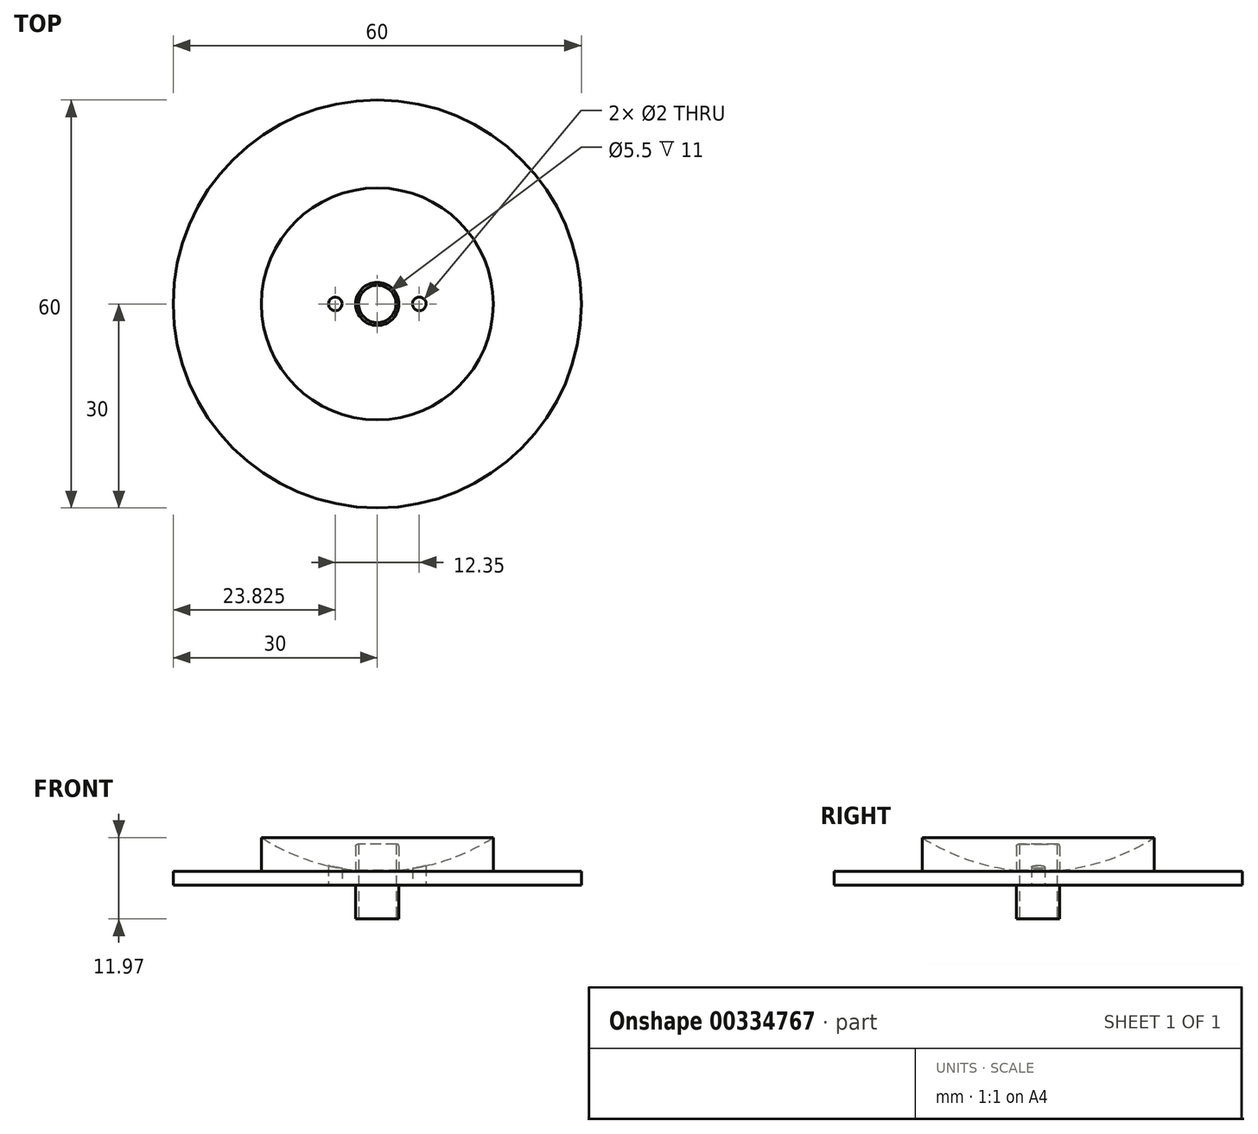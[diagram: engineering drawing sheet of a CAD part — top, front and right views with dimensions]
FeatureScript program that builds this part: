
annotation { "Feature Type Name" : "Feature", "Feature Type Description" : "" }
export const myFeature = defineFeature(function(context is Context, id is Id, definition is map)
    precondition{}
    {
        {
            var Q0;
            Q0=qCreatedBy(makeId("Front.planeOp"),FACE);
            var sketch = newSketch(context, id + "F0", { "sketchPlane" : qUnion([Q0])});
            skLineSegment(sketch, "E0.bottom", {"start": v(-30, 0) * mm, "end": v(30, 0) * mm});
            skLineSegment(sketch, "E0.top", {"start": v(-30, 2) * mm, "end": v(30, 2) * mm});
            skLineSegment(sketch, "E0.left", {"start": v(-30, 0) * mm, "end": v(-30, 2) * mm});
            skLineSegment(sketch, "E0.right", {"start": v(30, 0) * mm, "end": v(30, 2) * mm});
            skArc(sketch, "E1", {"start": v(-17.05, 6.97) * mm, "mid": v(0, 2) * mm, "end": v(17.05, 6.97) * mm});
            skLineSegment(sketch, "E2", {"start": v(-17.05, 6.97) * mm, "end": v(-17.05, 2) * mm});
            skLineSegment(sketch, "E3.MirrorCS", {"start": v(17.05, 6.97) * mm, "end": v(17.05, 2) * mm});
            skLineSegment(sketch, "E4", {"start": v(0, 65.5) * mm, "end": v(0, 0) * mm});
            skCircle(sketch, "E5", {"center": v(0, 33.75) * mm, "radius": 31.75 * mm});
            skSolve(sketch);
        }
        {
            var Q0;
            {var subQ0=sQuery(id+"F0.wireOp",EDGE,"E1");var subQ1=makeQuery(id+"F0.imprint","INTERSECT",VERTEX,{"derivedFrom":[subQ0,sQuery(id+"F0.wireOp",EDGE,"E3.MirrorCS")]});Q0=makeQuery(id+"F0.imprint","IMPRINT",FACE,{"disambiguationData":[TD([[makeQuery(id+"F0.imprint","IMPRINT",EDGE,{"disambiguationData":[TD([[subQ1,-1.0]])],"derivedFrom":subQ0}),1.0]])]});}
            var Q1;
            {var subQ0=sQuery(id+"F0.wireOp",EDGE,"E3.MirrorCS");Q1=makeQuery(id+"F0.imprint","IMPRINT",FACE,{"disambiguationData":[TD([[makeQuery(id+"F0.imprint","IMPRINT",EDGE,{"derivedFrom":subQ0}),-1.0]])]});}
            var Q2;
            {var subQ0=sQuery(id+"F0.wireOp",EDGE,"E0.right");Q2=makeQuery(id+"F0.imprint","IMPRINT",FACE,{"disambiguationData":[TD([[makeQuery(id+"F0.imprint","IMPRINT",EDGE,{"derivedFrom":subQ0}),1.0]])]});}
            var Q3;
            Q3=sQuery(id+"F0.wireOp",EDGE,"E4");
            revolve(context, id + "F1", {"entities" : qUnion([Q0, Q1, Q2]), "axis" : qUnion([Q3]), "revolveType" : RevolveType.FULL});
        }
        {
            var Q0;
            Q0=qCreatedBy(makeId("Top.planeOp"),FACE);
            var sketch = newSketch(context, id + "F2", { "sketchPlane" : qUnion([Q0])});
            skCircle(sketch, "E6", {"center": v(0, 0) * mm, "radius": 3.17 * mm});
            skCircle(sketch, "E7", {"center": v(0, 0) * mm, "radius": 2.75 * mm});
            skSolve(sketch);
        }
        {
            var Q0;
            Q0 = qSketchRegion(id + "F2", true);
            extrude(context, id + "F3", {"entities" : qUnion([Q0]), "operationType" : NewBodyOperationType.ADD, "depth" : 6 * mm, "hasSecondDirection" : true, "secondDirectionOppositeDirection" : true, "secondDirectionDepth" : 5 * mm});
        }
        {
            var Q0;
            Q0=makeQuery(id+"F3.opExtrude","CAP_EDGE",EDGE,{"disambiguationData":[OSD([sQuery(id+"F2.wireOp",EDGE,"E6")])],"isStart":false});
            fillet(context, id + "F4", {"entities" : qUnion([Q0]), "radius" : .3 * mm, "tangentPropagation" : true, "allowEdgeOverflow" : false});
        }
        {
            var Q0;
            Q0=makeQuery(id+"F3.boolean.opBoolean","SPLIT",FACE,{"disambiguationData":[TD([makeQuery(id+"F3.opExtrude","SWEPT_FACE",FACE,{"disambiguationData":[OSD([sQuery(id+"F2.wireOp",EDGE,"E7")])]})])],"derivedFrom":makeQuery(id+"F1.opRevolve","SWEPT_FACE",FACE,{"disambiguationData":[OSD([sQuery(id+"F0.wireOp",EDGE,"E0.bottom")])]})});
            var sketch = newSketch(context, id + "F5", { "sketchPlane" : qUnion([Q0])});
            skCircle(sketch, "E8", {"center": v(0, 0) * mm, "radius": 2.75 * mm});
            skSolve(sketch);
        }
        {
            var Q0;
            Q0 = qSketchRegion(id + "F5", true);
            extrude(context, id + "F6", {"entities" : qUnion([Q0]), "operationType" : NewBodyOperationType.REMOVE, "endBound" : BoundingType.THROUGH_ALL, "oppositeDirection" : true, "depth" : 25 * mm});
        }
        {
            var Q0;
            Q0=makeQuery(id+"F3.boolean.opBoolean","SPLIT",FACE,{"disambiguationData":[TD([makeQuery(id+"F1.opRevolve","SWEPT_FACE",FACE,{"disambiguationData":[OSD([sQuery(id+"F0.wireOp",EDGE,"E0.right")])]})])],"derivedFrom":makeQuery(id+"F1.opRevolve","SWEPT_FACE",FACE,{"disambiguationData":[OSD([sQuery(id+"F0.wireOp",EDGE,"E0.bottom")])]})});
            var sketch = newSketch(context, id + "F7", { "sketchPlane" : qUnion([Q0])});
            skPoint(sketch, "E9", {"position": v(-6.17, 0) * mm});
            skPoint(sketch, "E10", {"position": v(6.17, 0) * mm});
            skSolve(sketch);
        }
        {
            var Q0;
            Q0=sQuery(id+"F7.wireOp",VERTEX,"E9");
            var Q1;
            Q1=sQuery(id+"F7.wireOp",VERTEX,"E10");
            var Q2;
            Q2=makeQuery(id+"F1.opRevolve","SWEPT_BODY",BODY,{"disambiguationData":[OSD([sQuery(id+"F0.wireOp",EDGE,"E0.bottom"),sQuery(id+"F0.wireOp",EDGE,"E0.top"),sQuery(id+"F0.wireOp",EDGE,"E0.right"),sQuery(id+"F0.wireOp",EDGE,"E1"),sQuery(id+"F0.wireOp",EDGE,"E3.MirrorCS"),sQuery(id+"F0.wireOp",EDGE,"E4")])]});
            hole(context, id + "F8", {"style" : HoleStyle.SIMPLE, "endStyle" : HoleEndStyle.THROUGH, "holeDiameter" : 2 * mm, "tappedDepth" : 12 * mm, "tapClearance" : 3, "startFromSketch" : true, "locations" : qUnion([Q0, Q1]), "scope" : qUnion([Q2])});
        }
    });
